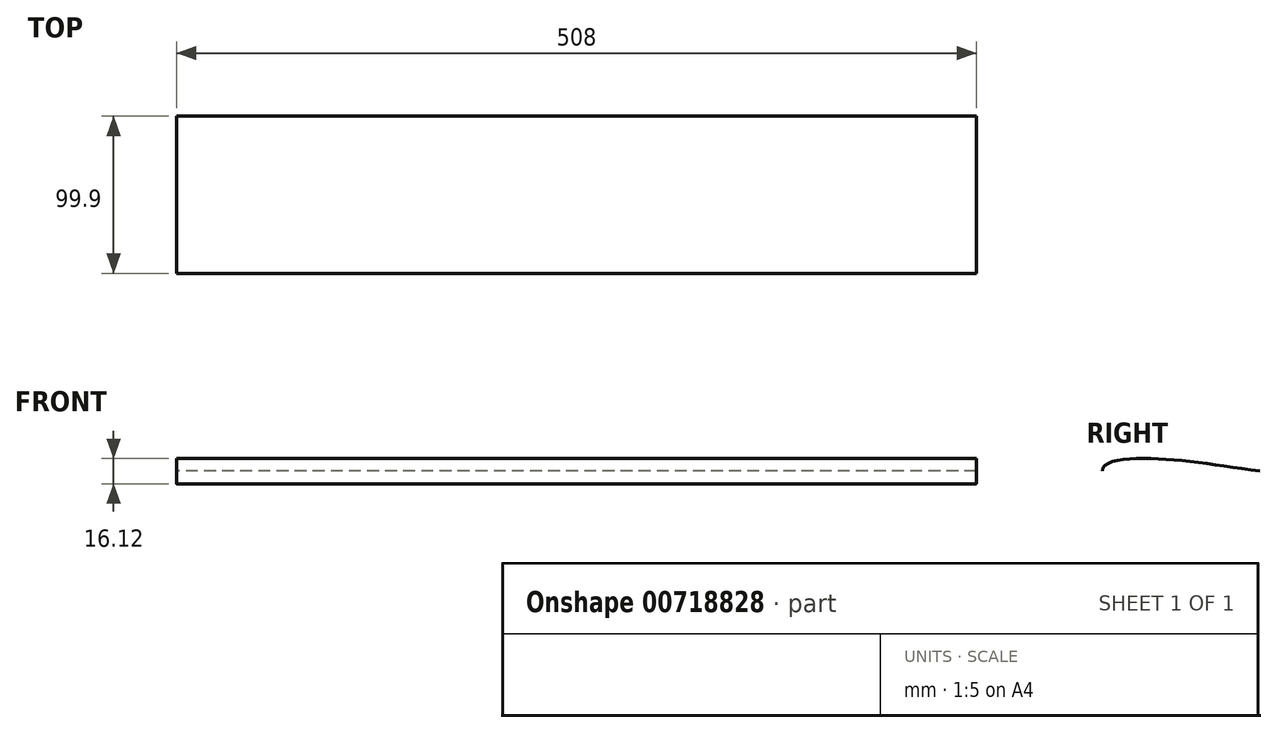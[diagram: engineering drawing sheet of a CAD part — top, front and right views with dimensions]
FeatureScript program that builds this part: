
annotation { "Feature Type Name" : "Feature", "Feature Type Description" : "" }
export const myFeature = defineFeature(function(context is Context, id is Id, definition is map)
    precondition{}
    {
        {
            var Q0;
            Q0=qCreatedBy(makeId("Right.planeOp"),FACE);
            var sketch = newSketch(context, id + "F0", { "sketchPlane" : qUnion([Q0])});
            skFitSpline(sketch, "E0", {"points": [v(-48.27, 0) * mm, v(-25.67, 8.03) * mm, v(51.63, 0) * mm], "startDerivative": vector(0, 50.2) * mm, "endDerivative": vector(131.66, -18.41) * mm});
            skFitSpline(sketch, "E1.MirrorCS", {"points": [v(-48.27, 0) * mm, v(-25.67, -8.03) * mm, v(51.63, 0) * mm], "startDerivative": vector(0, -50.2) * mm, "endDerivative": vector(131.66, 18.41) * mm});
            skSolve(sketch);
        }
        {
            var Q0;
            Q0=makeQuery(id+"F0.imprint","IMPRINT",FACE,{"disambiguationData":[TD([[makeQuery(id+"F0.imprint","IMPRINT",EDGE,{"derivedFrom":sQuery(id+"F0.wireOp",EDGE,"E0")}),-1.0]])]});
            extrude(context, id + "F1", {"entities" : qUnion([Q0]), "depth" : 508 * mm, "offsetDistance" : 25.4 * mm});
        }
    });
